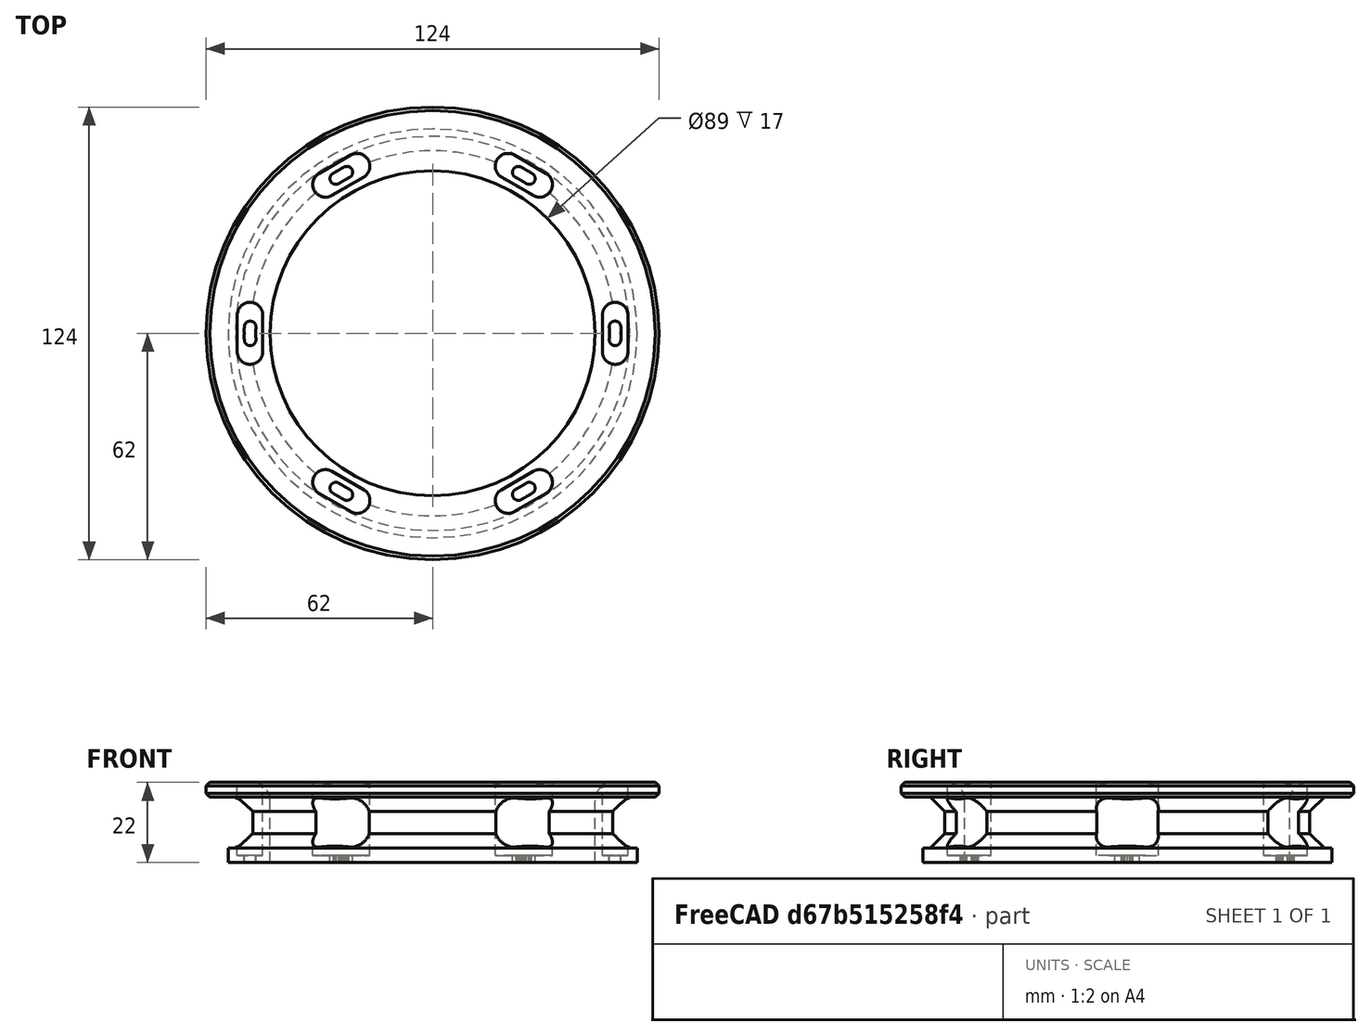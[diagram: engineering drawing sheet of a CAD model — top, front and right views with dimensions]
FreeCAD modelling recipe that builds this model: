
FCSTD DOCUMENT  (FreeCAD 0.15R4671 (Git))
Label: tendon_ring
License: All rights reserved
LicenseURL: http://en.wikipedia.org/wiki/All_rights_reserved
objects: Part::Cylinder×64, Part::MultiFuse×33, Part::Box×6, Part::Chamfer×4, Part::Cut×2, Part::Fillet×1
note: 110 computed .brp shape members not serialized (recipe doc carries the construction recipe); baked Part::Feature solids carry a one-line shape summary decoded from their .brp

FEATURE [Part::Cylinder] Cylinder
  Angle = 360
  Height = 4
  Radius = 56
FEATURE [Part::Cylinder] Cylinder001
  Angle = 360
  Height = 30
  Radius = 44.5
FEATURE [Part::Cylinder] Cylinder002
  Angle = 360
  Height = 14
  Placement = pos=(0,0,4) rot=(0,0,1;0rad)
  Radius = 50
FEATURE [Part::Cylinder] Cylinder003
  Angle = 360
  Height = 4
  Placement = pos=(0,0,18) rot=(0,0,1;0rad)
  Radius = 62
FEATURE [Part::MultiFuse] Fusion
  Shapes = -> [Cylinder,Cylinder002,Cylinder003]
FEATURE [Part::Cut] Cut
  Base = -> Fusion
  Tool = -> Cylinder001
FEATURE [Part::Chamfer] Chamfer
  Base = -> Cut
  Edges = 1 edges r=4: [Edge5]
FEATURE [Part::Chamfer] Chamfer001
  Base = -> Chamfer
  Edges = 1 edges r=4: [Edge8]
FEATURE [Part::Fillet] Fillet
  Base = -> Chamfer001
  Edges = 1 edges r=5: [Edge15]
FEATURE [Part::Cylinder] Cylinder004
  Angle = 360
  Height = 10
  Placement = pos=(50,0,-2) rot=(0,0,1;0rad)
  Radius = 1.6
FEATURE [Part::Cylinder] Cylinder005
  Angle = 360
  Height = 10
  Placement = pos=(-50,0,-2) rot=(0,0,1;0rad)
  Radius = 1.6
FEATURE [Part::MultiFuse] Fusion001
  Placement = pos=(0,0,0) rot=(0,0,1;0.017453rad)
  Shapes = -> [Cylinder004,Cylinder005]
FEATURE [Part::Cylinder] Cylinder006
  Angle = 360
  Height = 10
  Placement = pos=(50,0,-2) rot=(0,0,1;0rad)
  Radius = 1.6
FEATURE [Part::Cylinder] Cylinder007
  Angle = 360
  Height = 10
  Placement = pos=(-50,0,-2) rot=(0,0,1;0rad)
  Radius = 1.6
FEATURE [Part::MultiFuse] Fusion002
  Placement = pos=(0,0,0) rot=(0,0,1;0.034907rad)
  Shapes = -> [Cylinder006,Cylinder007]
FEATURE [Part::Cylinder] Cylinder008
  Angle = 360
  Height = 10
  Placement = pos=(50,0,-2) rot=(0,0,1;0rad)
  Radius = 1.6
FEATURE [Part::Cylinder] Cylinder009
  Angle = 360
  Height = 10
  Placement = pos=(-50,0,-2) rot=(0,0,1;0rad)
  Radius = 1.6
FEATURE [Part::MultiFuse] Fusion003
  Placement = pos=(0,0,0) rot=(0,0,-1;0.017453rad)
  Shapes = -> [Cylinder008,Cylinder009]
FEATURE [Part::Cylinder] Cylinder010
  Angle = 360
  Height = 10
  Placement = pos=(50,0,-2) rot=(0,0,1;0rad)
  Radius = 1.6
FEATURE [Part::Cylinder] Cylinder011
  Angle = 360
  Height = 10
  Placement = pos=(-50,0,-2) rot=(0,0,1;0rad)
  Radius = 1.6
FEATURE [Part::MultiFuse] Fusion004
  Placement = pos=(0,0,0) rot=(0,0,-1;0.034907rad)
  Shapes = -> [Cylinder010,Cylinder011]
FEATURE [Part::Cylinder] Cylinder012
  Angle = 360
  Height = 10
  Placement = pos=(50,0,-2) rot=(0,0,1;0rad)
  Radius = 1.6
FEATURE [Part::Cylinder] Cylinder013
  Angle = 360
  Height = 10
  Placement = pos=(-50,0,-2) rot=(0,0,1;0rad)
  Radius = 1.6
FEATURE [Part::MultiFuse] Fusion005
  Placement = pos=(0,0,0) rot=(0,0,-1;0.008727rad)
  Shapes = -> [Cylinder012,Cylinder013]
FEATURE [Part::Cylinder] Cylinder014
  Angle = 360
  Height = 10
  Placement = pos=(50,0,-2) rot=(0,0,1;0rad)
  Radius = 1.6
FEATURE [Part::Cylinder] Cylinder015
  Angle = 360
  Height = 10
  Placement = pos=(-50,0,-2) rot=(0,0,1;0rad)
  Radius = 1.6
FEATURE [Part::MultiFuse] Fusion006
  Placement = pos=(0,0,0) rot=(0,0,-1;0.02618rad)
  Shapes = -> [Cylinder014,Cylinder015]
FEATURE [Part::Cylinder] Cylinder016
  Angle = 360
  Height = 10
  Placement = pos=(50,0,-2) rot=(0,0,1;0rad)
  Radius = 1.6
FEATURE [Part::Cylinder] Cylinder017
  Angle = 360
  Height = 10
  Placement = pos=(-50,0,-2) rot=(0,0,1;0rad)
  Radius = 1.6
FEATURE [Part::MultiFuse] Fusion007
  Placement = pos=(0,0,0) rot=(0,0,1;0.02618rad)
  Shapes = -> [Cylinder016,Cylinder017]
FEATURE [Part::Cylinder] Cylinder018
  Angle = 360
  Height = 10
  Placement = pos=(50,0,-2) rot=(0,0,1;0rad)
  Radius = 1.6
FEATURE [Part::Cylinder] Cylinder019
  Angle = 360
  Height = 10
  Placement = pos=(-50,0,-2) rot=(0,0,1;0rad)
  Radius = 1.6
FEATURE [Part::MultiFuse] Fusion008
  Placement = pos=(0,0,0) rot=(0,0,1;0.008727rad)
  Shapes = -> [Cylinder018,Cylinder019]
FEATURE [Part::MultiFuse] Fusion009
  Shapes = -> [Fusion004,Fusion007,Fusion002,Fusion006,Fusion003,Fusion005,Fusion001,Fusion008]
FEATURE [Part::Cylinder] Cylinder020
  Angle = 360
  Height = 10
  Placement = pos=(50,0,-2) rot=(0,0,1;0rad)
  Radius = 1.6
FEATURE [Part::Cylinder] Cylinder021
  Angle = 360
  Height = 10
  Placement = pos=(-50,0,-2) rot=(0,0,1;0rad)
  Radius = 1.6
FEATURE [Part::MultiFuse] Fusion010
  Placement = pos=(0,0,0) rot=(0,0,1;0.017453rad)
  Shapes = -> [Cylinder020,Cylinder021]
FEATURE [Part::Cylinder] Cylinder022
  Angle = 360
  Height = 10
  Placement = pos=(50,0,-2) rot=(0,0,1;0rad)
  Radius = 1.6
FEATURE [Part::Cylinder] Cylinder023
  Angle = 360
  Height = 10
  Placement = pos=(-50,0,-2) rot=(0,0,1;0rad)
  Radius = 1.6
FEATURE [Part::MultiFuse] Fusion011
  Placement = pos=(0,0,0) rot=(0,0,1;0.034907rad)
  Shapes = -> [Cylinder022,Cylinder023]
FEATURE [Part::Cylinder] Cylinder024
  Angle = 360
  Height = 10
  Placement = pos=(50,0,-2) rot=(0,0,1;0rad)
  Radius = 1.6
FEATURE [Part::Cylinder] Cylinder025
  Angle = 360
  Height = 10
  Placement = pos=(-50,0,-2) rot=(0,0,1;0rad)
  Radius = 1.6
FEATURE [Part::MultiFuse] Fusion012
  Placement = pos=(0,0,0) rot=(0,0,-1;0.017453rad)
  Shapes = -> [Cylinder024,Cylinder025]
FEATURE [Part::Cylinder] Cylinder026
  Angle = 360
  Height = 10
  Placement = pos=(50,0,-2) rot=(0,0,1;0rad)
  Radius = 1.6
FEATURE [Part::Cylinder] Cylinder027
  Angle = 360
  Height = 10
  Placement = pos=(-50,0,-2) rot=(0,0,1;0rad)
  Radius = 1.6
FEATURE [Part::MultiFuse] Fusion013
  Placement = pos=(0,0,0) rot=(0,0,-1;0.034907rad)
  Shapes = -> [Cylinder026,Cylinder027]
FEATURE [Part::Cylinder] Cylinder028
  Angle = 360
  Height = 10
  Placement = pos=(50,0,-2) rot=(0,0,1;0rad)
  Radius = 1.6
FEATURE [Part::Cylinder] Cylinder029
  Angle = 360
  Height = 10
  Placement = pos=(-50,0,-2) rot=(0,0,1;0rad)
  Radius = 1.6
FEATURE [Part::MultiFuse] Fusion014
  Placement = pos=(0,0,0) rot=(0,0,-1;0.008727rad)
  Shapes = -> [Cylinder028,Cylinder029]
FEATURE [Part::Cylinder] Cylinder030
  Angle = 360
  Height = 10
  Placement = pos=(50,0,-2) rot=(0,0,1;0rad)
  Radius = 1.6
FEATURE [Part::Cylinder] Cylinder031
  Angle = 360
  Height = 10
  Placement = pos=(-50,0,-2) rot=(0,0,1;0rad)
  Radius = 1.6
FEATURE [Part::MultiFuse] Fusion015
  Placement = pos=(0,0,0) rot=(0,0,-1;0.02618rad)
  Shapes = -> [Cylinder030,Cylinder031]
FEATURE [Part::Cylinder] Cylinder032
  Angle = 360
  Height = 10
  Placement = pos=(50,0,-2) rot=(0,0,1;0rad)
  Radius = 1.6
FEATURE [Part::Cylinder] Cylinder033
  Angle = 360
  Height = 10
  Placement = pos=(-50,0,-2) rot=(0,0,1;0rad)
  Radius = 1.6
FEATURE [Part::MultiFuse] Fusion016
  Placement = pos=(0,0,0) rot=(0,0,1;0.02618rad)
  Shapes = -> [Cylinder032,Cylinder033]
FEATURE [Part::Cylinder] Cylinder034
  Angle = 360
  Height = 10
  Placement = pos=(50,0,-2) rot=(0,0,1;0rad)
  Radius = 1.6
FEATURE [Part::Cylinder] Cylinder035
  Angle = 360
  Height = 10
  Placement = pos=(-50,0,-2) rot=(0,0,1;0rad)
  Radius = 1.6
FEATURE [Part::MultiFuse] Fusion017
  Placement = pos=(0,0,0) rot=(0,0,1;0.008727rad)
  Shapes = -> [Cylinder034,Cylinder035]
FEATURE [Part::MultiFuse] Fusion018
  Placement = pos=(0,0,0) rot=(0,0,1;1.0472rad)
  Shapes = -> [Fusion013,Fusion016,Fusion011,Fusion015,Fusion012,Fusion014,Fusion010,Fusion017]
FEATURE [Part::Cylinder] Cylinder036
  Angle = 360
  Height = 10
  Placement = pos=(50,0,-2) rot=(0,0,1;0rad)
  Radius = 1.6
FEATURE [Part::Cylinder] Cylinder037
  Angle = 360
  Height = 10
  Placement = pos=(-50,0,-2) rot=(0,0,1;0rad)
  Radius = 1.6
FEATURE [Part::MultiFuse] Fusion019
  Placement = pos=(0,0,0) rot=(0,0,1;0.017453rad)
  Shapes = -> [Cylinder036,Cylinder037]
FEATURE [Part::Cylinder] Cylinder038
  Angle = 360
  Height = 10
  Placement = pos=(50,0,-2) rot=(0,0,1;0rad)
  Radius = 1.6
FEATURE [Part::Cylinder] Cylinder039
  Angle = 360
  Height = 10
  Placement = pos=(-50,0,-2) rot=(0,0,1;0rad)
  Radius = 1.6
FEATURE [Part::MultiFuse] Fusion020
  Placement = pos=(0,0,0) rot=(0,0,1;0.034907rad)
  Shapes = -> [Cylinder038,Cylinder039]
FEATURE [Part::Cylinder] Cylinder040
  Angle = 360
  Height = 10
  Placement = pos=(50,0,-2) rot=(0,0,1;0rad)
  Radius = 1.6
FEATURE [Part::Cylinder] Cylinder041
  Angle = 360
  Height = 10
  Placement = pos=(-50,0,-2) rot=(0,0,1;0rad)
  Radius = 1.6
FEATURE [Part::MultiFuse] Fusion021
  Placement = pos=(0,0,0) rot=(0,0,-1;0.017453rad)
  Shapes = -> [Cylinder040,Cylinder041]
FEATURE [Part::Cylinder] Cylinder042
  Angle = 360
  Height = 10
  Placement = pos=(50,0,-2) rot=(0,0,1;0rad)
  Radius = 1.6
FEATURE [Part::Cylinder] Cylinder043
  Angle = 360
  Height = 10
  Placement = pos=(-50,0,-2) rot=(0,0,1;0rad)
  Radius = 1.6
FEATURE [Part::MultiFuse] Fusion022
  Placement = pos=(0,0,0) rot=(0,0,-1;0.034907rad)
  Shapes = -> [Cylinder042,Cylinder043]
FEATURE [Part::Cylinder] Cylinder044
  Angle = 360
  Height = 10
  Placement = pos=(50,0,-2) rot=(0,0,1;0rad)
  Radius = 1.6
FEATURE [Part::Cylinder] Cylinder045
  Angle = 360
  Height = 10
  Placement = pos=(-50,0,-2) rot=(0,0,1;0rad)
  Radius = 1.6
FEATURE [Part::MultiFuse] Fusion023
  Placement = pos=(0,0,0) rot=(0,0,-1;0.008727rad)
  Shapes = -> [Cylinder044,Cylinder045]
FEATURE [Part::Cylinder] Cylinder046
  Angle = 360
  Height = 10
  Placement = pos=(50,0,-2) rot=(0,0,1;0rad)
  Radius = 1.6
FEATURE [Part::Cylinder] Cylinder047
  Angle = 360
  Height = 10
  Placement = pos=(-50,0,-2) rot=(0,0,1;0rad)
  Radius = 1.6
FEATURE [Part::MultiFuse] Fusion024
  Placement = pos=(0,0,0) rot=(0,0,-1;0.02618rad)
  Shapes = -> [Cylinder046,Cylinder047]
FEATURE [Part::Cylinder] Cylinder048
  Angle = 360
  Height = 10
  Placement = pos=(50,0,-2) rot=(0,0,1;0rad)
  Radius = 1.6
FEATURE [Part::Cylinder] Cylinder049
  Angle = 360
  Height = 10
  Placement = pos=(-50,0,-2) rot=(0,0,1;0rad)
  Radius = 1.6
FEATURE [Part::MultiFuse] Fusion025
  Placement = pos=(0,0,0) rot=(0,0,1;0.02618rad)
  Shapes = -> [Cylinder048,Cylinder049]
FEATURE [Part::Cylinder] Cylinder050
  Angle = 360
  Height = 10
  Placement = pos=(50,0,-2) rot=(0,0,1;0rad)
  Radius = 1.6
FEATURE [Part::Cylinder] Cylinder051
  Angle = 360
  Height = 10
  Placement = pos=(-50,0,-2) rot=(0,0,1;0rad)
  Radius = 1.6
FEATURE [Part::MultiFuse] Fusion026
  Placement = pos=(0,0,0) rot=(0,0,1;0.008727rad)
  Shapes = -> [Cylinder050,Cylinder051]
FEATURE [Part::MultiFuse] Fusion027
  Placement = pos=(0,0,0) rot=(0,0,1;2.0944rad)
  Shapes = -> [Fusion022,Fusion025,Fusion020,Fusion024,Fusion021,Fusion023,Fusion019,Fusion026]
FEATURE [Part::MultiFuse] Fusion028
  Shapes = -> [Fusion027,Fusion018,Fusion009]
FEATURE [Part::Box] Box009  label="Cube010"
  Height = 30
  Length = 10
  Placement = pos=(-5,46.5,2) rot=(0,0,1;0rad)
  Width = 7
FEATURE [Part::Box] Box010  label="Cube011"
  Height = 30
  Length = 10
  Placement = pos=(-5,-53.5,2) rot=(0,0,1;0rad)
  Width = 7
FEATURE [Part::Cylinder] Cylinder064
  Angle = 360
  Height = 30
  Placement = pos=(-5,50,2) rot=(0,0,1;0rad)
  Radius = 3.5
FEATURE [Part::Cylinder] Cylinder065
  Angle = 360
  Height = 30
  Placement = pos=(5,50,2) rot=(0,0,1;0rad)
  Radius = 3.5
FEATURE [Part::Cylinder] Cylinder066
  Angle = 360
  Height = 30
  Placement = pos=(5,-50,2) rot=(0,0,1;0rad)
  Radius = 3.5
FEATURE [Part::Cylinder] Cylinder067
  Angle = 360
  Height = 30
  Placement = pos=(-5,-50,2) rot=(0,0,1;0rad)
  Radius = 3.5
FEATURE [Part::MultiFuse] Fusion032
  Placement = pos=(0,0,0) rot=(0,0,1;2.61799rad)
  Shapes = -> [Cylinder064,Cylinder065,Cylinder066,Cylinder067,Box009,Box010]
FEATURE [Part::Box] Box  label="Cube012"
  Height = 30
  Length = 10
  Placement = pos=(-5,46.5,2) rot=(0,0,1;0rad)
  Width = 7
FEATURE [Part::Box] Box011  label="Cube013"
  Height = 30
  Length = 10
  Placement = pos=(-5,-53.5,2) rot=(0,0,1;0rad)
  Width = 7
FEATURE [Part::Cylinder] Cylinder068
  Angle = 360
  Height = 30
  Placement = pos=(-5,50,2) rot=(0,0,1;0rad)
  Radius = 3.5
FEATURE [Part::Cylinder] Cylinder069
  Angle = 360
  Height = 30
  Placement = pos=(5,50,2) rot=(0,0,1;0rad)
  Radius = 3.5
FEATURE [Part::Cylinder] Cylinder070
  Angle = 360
  Height = 30
  Placement = pos=(5,-50,2) rot=(0,0,1;0rad)
  Radius = 3.5
FEATURE [Part::Cylinder] Cylinder071
  Angle = 360
  Height = 30
  Placement = pos=(-5,-50,2) rot=(0,0,1;0rad)
  Radius = 3.5
FEATURE [Part::MultiFuse] Fusion033
  Placement = pos=(0,0,0) rot=(0,0,1;0.523599rad)
  Shapes = -> [Cylinder068,Cylinder069,Cylinder070,Cylinder071,Box,Box011]
FEATURE [Part::Box] Box012  label="Cube014"
  Height = 30
  Length = 10
  Placement = pos=(-5,46.5,2) rot=(0,0,1;0rad)
  Width = 7
FEATURE [Part::Box] Box013  label="Cube015"
  Height = 30
  Length = 10
  Placement = pos=(-5,-53.5,2) rot=(0,0,1;0rad)
  Width = 7
FEATURE [Part::Cylinder] Cylinder072
  Angle = 360
  Height = 30
  Placement = pos=(-5,50,2) rot=(0,0,1;0rad)
  Radius = 3.5
FEATURE [Part::Cylinder] Cylinder073
  Angle = 360
  Height = 30
  Placement = pos=(5,50,2) rot=(0,0,1;0rad)
  Radius = 3.5
FEATURE [Part::Cylinder] Cylinder074
  Angle = 360
  Height = 30
  Placement = pos=(5,-50,2) rot=(0,0,1;0rad)
  Radius = 3.5
FEATURE [Part::Cylinder] Cylinder075
  Angle = 360
  Height = 30
  Placement = pos=(-5,-50,2) rot=(0,0,1;0rad)
  Radius = 3.5
FEATURE [Part::MultiFuse] Fusion034
  Placement = pos=(0,0,0) rot=(0,0,1;1.5708rad)
  Shapes = -> [Cylinder072,Cylinder073,Cylinder074,Cylinder075,Box012,Box013]
FEATURE [Part::MultiFuse] Fusion035
  Shapes = -> [Fusion032,Fusion033,Fusion028,Fusion034]
FEATURE [Part::Cut] Cut001
  Base = -> Fillet
  Tool = -> Fusion035
FEATURE [Part::Chamfer] Chamfer002
  Base = -> Cut001
  Edges = 1 edges r=1: [Edge33]
FEATURE [Part::Chamfer] Chamfer003
  Base = -> Chamfer002
  Edges = 1 edges r=1: [Edge3]
